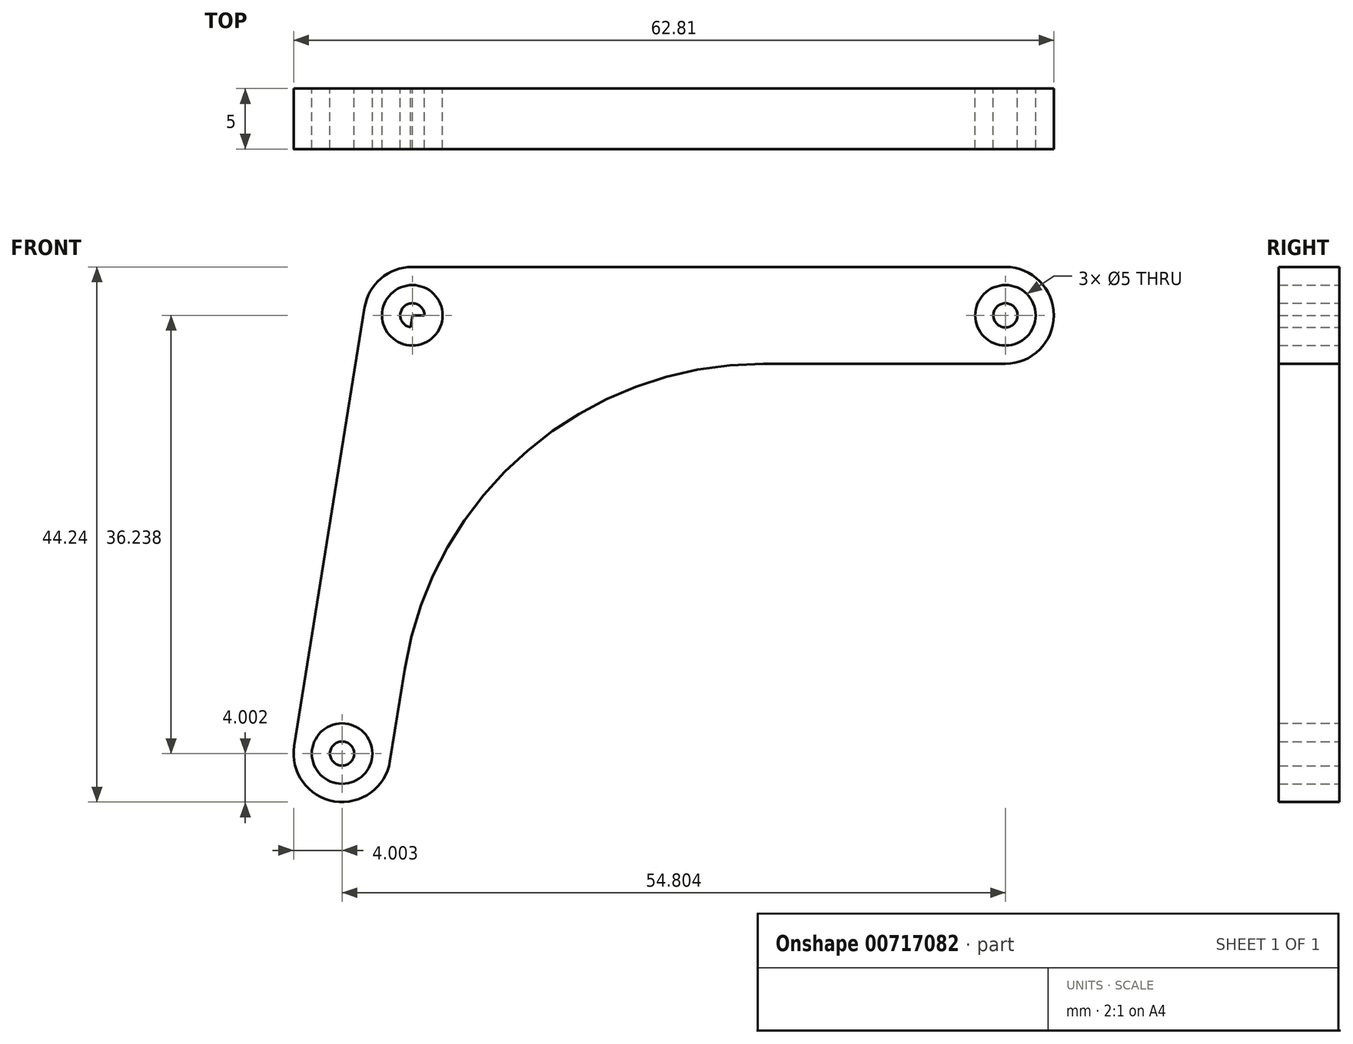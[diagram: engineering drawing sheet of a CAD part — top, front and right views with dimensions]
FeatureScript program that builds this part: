
annotation { "Feature Type Name" : "Feature", "Feature Type Description" : "" }
export const myFeature = defineFeature(function(context is Context, id is Id, definition is map)
    precondition{}
    {
        {
            var Q0;
            Q0=qCreatedBy(makeId("Front.planeOp"),FACE);
            var sketch = newSketch(context, id + "F0", { "sketchPlane" : qUnion([Q0])});
            skCircle(sketch, "E0", {"center": v(-21.78, 19.26) * mm, "radius": 2.5 * mm});
            skArc(sketch, "E1", {"start": v(-21.78, 23.26) * mm, "mid": v(-24.38, 22.3) * mm, "end": v(-25.73, 19.9) * mm});
            skCircle(sketch, "E2", {"center": v(-27.59, -16.98) * mm, "radius": 2.5 * mm});
            skArc(sketch, "E3", {"start": v(-31.54, -16.35) * mm, "mid": v(-28.22, -20.93) * mm, "end": v(-23.64, -17.61) * mm});
            skCircle(sketch, "E4", {"center": v(27.22, 19.26) * mm, "radius": 2.5 * mm});
            skArc(sketch, "E5", {"start": v(27.22, 15.26) * mm, "mid": v(31.22, 19.26) * mm, "end": v(27.22, 23.26) * mm});
            skLineSegment(sketch, "E6", {"start": v(-21.78, 19.26) * mm, "end": v(27.22, 19.26) * mm});
            skLineSegment(sketch, "E7", {"start": v(-21.78, 19.26) * mm, "end": v(-27.59, -16.98) * mm});
            skLineSegment(sketch, "E8.0", {"start": v(7.2, 15.26) * mm, "end": v(27.86, 15.26) * mm});
            skLineSegment(sketch, "E9.0", {"start": v(-21.78, 23.26) * mm, "end": v(27.86, 23.26) * mm});
            skLineSegment(sketch, "E9.1", {"start": v(-25.73, 19.9) * mm, "end": v(-31.64, -16.98) * mm});
            skLineSegment(sketch, "E10.0", {"start": v(-22.42, -10) * mm, "end": v(-23.64, -17.61) * mm});
            skLineSegment(sketch, "E10.1", {"start": v(7.2, 15.26) * mm, "end": v(27.22, 15.26) * mm});
            skPoint(sketch, "E11.visualSharp", {"position": v(-18.37, 15.26) * mm});
            skArc(sketch, "E11.filletArc", {"start": v(7.2, 15.26) * mm, "mid": v(-12.26, 8.09) * mm, "end": v(-22.42, -10) * mm});
            skCircle(sketch, "E12", {"center": v(-27.59, -16.98) * mm, "radius": 1 * mm});
            skCircle(sketch, "E13", {"center": v(27.22, 19.26) * mm, "radius": 1 * mm});
            skCircle(sketch, "E14", {"center": v(-21.78, 19.26) * mm, "radius": 1 * mm});
            skSolve(sketch);
        }
        {
            var Q0;
            {var subQ1=sQuery(id+"F0.wireOp",EDGE,"E1");Q0=makeQuery(id+"F0.imprint","IMPRINT",FACE,{"disambiguationData":[TD([[makeQuery(id+"F0.imprint","IMPRINT",EDGE,{"derivedFrom":subQ1}),1.0]])]});}
            extrude(context, id + "F1", {"entities" : qUnion([Q0]), "depth" : 5 * mm, "offsetDistance" : 25.4 * mm});
        }
        {
            var Q0;
            {var subQ0=sQuery(id+"F0.wireOp",EDGE,"E7");var subQ1=sQuery(id+"F0.wireOp",EDGE,"E6");var subQ2=makeQuery(id+"F0.imprint","INTERSECT",VERTEX,{"derivedFrom":[subQ1,subQ0]});Q0=makeQuery(id+"F0.imprint","IMPRINT",FACE,{"disambiguationData":[TD([[makeQuery(id+"F0.imprint","IMPRINT",EDGE,{"disambiguationData":[TD([[subQ2,-1.0]])],"derivedFrom":subQ1}),1.0]])]});}
            var Q1;
            Q1=makeQuery(id+"F0.imprint","IMPRINT",FACE,{"disambiguationData":[TD([[makeQuery(id+"F0.imprint","IMPRINT",EDGE,{"derivedFrom":sQuery(id+"F0.wireOp",EDGE,"E13")}),1.0]])]});
            var Q2;
            Q2=makeQuery(id+"F0.imprint","IMPRINT",FACE,{"disambiguationData":[TD([[makeQuery(id+"F0.imprint","IMPRINT",EDGE,{"derivedFrom":sQuery(id+"F0.wireOp",EDGE,"E12")}),1.0]])]});
            extrude(context, id + "F2", {"entities" : qUnion([Q0, Q1, Q2]), "depth" : 5 * mm, "offsetDistance" : 25.4 * mm});
        }
    });
